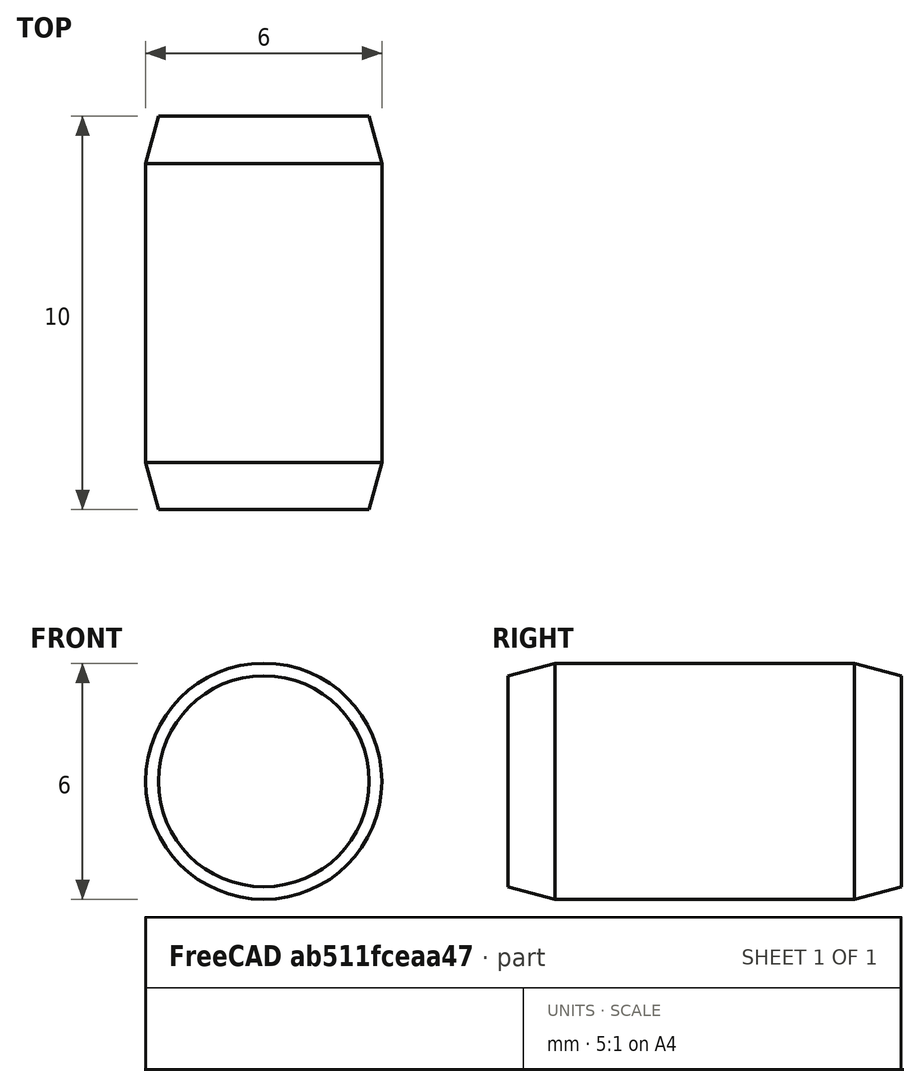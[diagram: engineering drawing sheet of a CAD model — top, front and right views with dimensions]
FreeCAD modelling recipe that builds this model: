
FCSTD DOCUMENT  (FreeCAD 0.15R4470 (Git))
Label: Zyl-Stift_ISO_8734-6x10
License: CC-BY 3.0
LicenseURL: http://creativecommons.org/licenses/by/3.0/
objects: Sketcher::SketchObject×1, PartDesign::Revolution×1
note: 3 computed .brp shape members not serialized (recipe doc carries the construction recipe); baked Part::Feature solids carry a one-line shape summary decoded from their .brp

FEATURE [Sketcher::SketchObject] Sketch
  Placement = pos=(0,0,0) rot=(0.57735,0.57735,0.57735;2.0944rad)
  sketch-geometry (7):
    g0: LineSegment StartX=0 StartY=0 StartZ=0 EndX=0 EndY=2.67846 EndZ=0
    g1: LineSegment StartX=0 StartY=2.67846 StartZ=0 EndX=1.2 EndY=3 EndZ=0
    g2: LineSegment StartX=1.2 StartY=3 StartZ=0 EndX=8.8 EndY=3 EndZ=0
    g3: LineSegment StartX=8.8 StartY=3 StartZ=0 EndX=10 EndY=2.67846 EndZ=0
    g4: LineSegment StartX=10 StartY=2.67846 StartZ=0 EndX=10 EndY=0 EndZ=0
    g5: LineSegment StartX=10 StartY=0 StartZ=0 EndX=0 EndY=0 EndZ=0
    g6: LineSegment [constr] StartX=0 StartY=2.67846 StartZ=0 EndX=10 EndY=2.67846 EndZ=0
  constraints (19):
    c: Coincident(g0,g-1)
    c: PointOnObject(g0,g-2)
    c: Coincident(g0,g1)
    c: Coincident(g1,g2)
    c: Horizontal(g2)
    c: Coincident(g2,g3)
    c: Coincident(g3,g4)
    c: Vertical(g4)
    c: Coincident(g4,g5)
    c: Coincident(g5,g-1)
    c: Horizontal(g5)
    c: Equal(g3,g1)
    c: Coincident(g6,g0)
    c: Coincident(g6,g3)
    c: Horizontal(g6)
    c: Angle(g6,g1) = 0.261799
    c: DistanceY(g-1,g1) = 3
    c: DistanceX(g5) = -10
    c: DistanceX(g1) = 1.2
FEATURE [PartDesign::Revolution] Revolution  label="Zyl-Stift ISO 8734-6x10 #"
  Angle = 360
  Axis = (0,1,0)
  Base = (0,0,0)
  Placement = pos=(0,0,0) rot=(0.57735,0.57735,0.57735;2.0944rad)
  ReferenceAxis = -> Sketch [H_Axis]
  Sketch = -> Sketch
